# Revit family: МПА_В_700_А31_Eng
name_source: partatom
category: Mechanical Equipment
units: mm (PartAtom-declared; Revit-internal decimal feet)

## family parameters
Always vertical = Yes
Classification = None
Cut with Voids When Loaded = No
Part Type = Normal
Room Calculation Point = No
Round Connector Dimension = Use Diameter
Shared = No
Work Plane-Based = No

## types (2) — shared parameters
00_20_Manufacturer = Vents
00_20_Name = Air supply unit
Amperage = 1 A
Apparent Load = 242 W
B = 460 mm  [stored 1.50919 ft]
B1 = 353 mm  [stored 1.15814 ft]
B2 = 565 mm  [stored 1.85367 ft]
Casing Material = Steel, galvanized
D = 250 mm  [stored 0.82021 ft]
Diameter = 250 mm  [stored 0.82021 ft]
Dy = 245 mm  [stored 0.803806 ft]
E = 330 mm
Filter = Coarse 90%/G4
Frequency = 50 Hz
H = 370 mm  [stored 1.21391 ft]
H1 = 351 mm  [stored 1.15157 ft]
Height = 370 mm  [stored 1.21391 ft]
L = 972 mm
L1 = 850 mm  [stored 2.78871 ft]
L3 = 160 mm  [stored 0.524934 ft]
L4 = 225 mm  [stored 0.738189 ft]
L5 = 400 mm  [stored 1.31234 ft]
Length = 972 mm
Load Classification = HVAC
Maintenance zone material = <By Category>
Manufacturer = Vents
Maximum Air Flow = 800.0 m³/h
Number of Fase = 1
Power = 139 W
Sound pressure level at 3 m distance = 44 dBA
URL = https://ventilation-system.com
Voltage = 230 V
Weight = 27.00 kg
Width = 565 mm  [stored 1.85367 ft]
b1 = 177 mm
zero-valued in all types: Default Elevation

## per-type parameters (varying)
| type | BE | BW1 | BW2 | BW3 | Left | Right |
| MPA 700 W ЕС L А31 | 613 mm | 580 mm  [stored 1.90289 ft] | 100 mm  [stored 0.328084 ft] | 565 mm  [stored 1.85367 ft] | Yes | No |
| MPA 700 W ЕС R А31 | 48 mm  [stored 0.15748 ft] | 560 mm  [stored 1.83727 ft] | 80 mm  [stored 0.262467 ft] | 95 mm | No | Yes |

note: column(s) folded — value = type name in every type: 00_20_Type

note: [stored X ft] marks values corroborated as IEEE doubles in the binary element streams (Revit-internal decimal feet)
